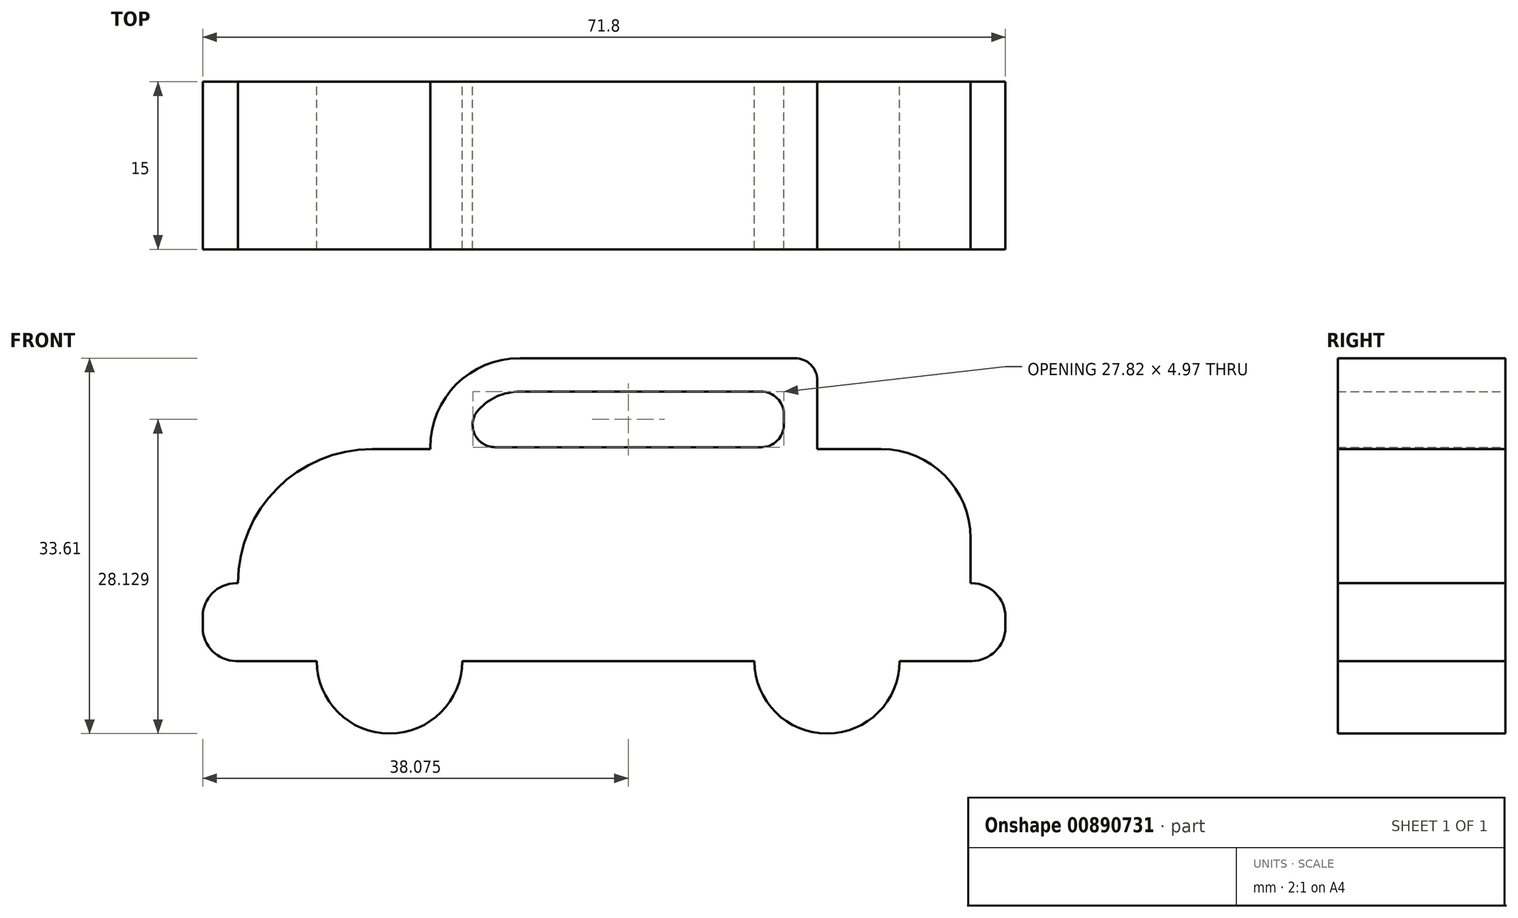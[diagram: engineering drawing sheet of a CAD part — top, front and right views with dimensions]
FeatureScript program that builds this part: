
annotation { "Feature Type Name" : "Feature", "Feature Type Description" : "" }
export const myFeature = defineFeature(function(context is Context, id is Id, definition is map)
    precondition{}
    {
        {
            var Q0;
            Q0=qCreatedBy(makeId("Front.planeOp"),FACE);
            var sketch = newSketch(context, id + "F0", { "sketchPlane" : qUnion([Q0])});
            skLineSegment(sketch, "E0.bottom", {"start": v(-41.37, 0) * mm, "end": v(-34.15, 0) * mm});
            skLineSegment(sketch, "E0.top", {"start": v(-41.37, 6.96) * mm, "end": v(-41.22, 6.96) * mm});
            skLineSegment(sketch, "E0.left", {"start": v(-44.37, 3) * mm, "end": v(-44.37, 3.96) * mm});
            skLineSegment(sketch, "E0.right", {"start": v(27.43, 3) * mm, "end": v(27.43, 3.96) * mm});
            skLineSegment(sketch, "E1", {"start": v(-41.22, 6.96) * mm, "end": v(-41.22, 6.97) * mm});
            skLineSegment(sketch, "E2", {"start": v(-29.22, 18.97) * mm, "end": v(-24.01, 18.97) * mm});
            skLineSegment(sketch, "E3", {"start": v(-24.01, 18.97) * mm, "end": v(-24.01, 19.11) * mm});
            skLineSegment(sketch, "E4", {"start": v(-16.01, 27.11) * mm, "end": v(8.62, 27.11) * mm});
            skLineSegment(sketch, "E5", {"start": v(10.62, 25.11) * mm, "end": v(10.62, 18.97) * mm});
            skLineSegment(sketch, "E6", {"start": v(10.62, 18.97) * mm, "end": v(16.33, 18.97) * mm});
            skLineSegment(sketch, "E7", {"start": v(24.33, 10.97) * mm, "end": v(24.33, 6.96) * mm});
            skLineSegment(sketch, "E8.trimOffspring", {"start": v(24.33, 6.96) * mm, "end": v(24.43, 6.96) * mm});
            skArc(sketch, "E9", {"start": v(-34.15, 0) * mm, "mid": v(-27.65, -6.5) * mm, "end": v(-21.15, 0) * mm});
            skArc(sketch, "E10", {"start": v(4.98, 0) * mm, "mid": v(11.48, -6.5) * mm, "end": v(17.98, 0) * mm});
            skLineSegment(sketch, "E11.trimOffspring", {"start": v(-21.15, 0) * mm, "end": v(4.98, 0) * mm});
            skLineSegment(sketch, "E12.trimOffspring", {"start": v(17.98, 0) * mm, "end": v(24.43, 0) * mm});
            skPoint(sketch, "E13.visualSharp", {"position": v(-44.37, 0) * mm});
            skArc(sketch, "E13.filletArc", {"start": v(-44.37, 3) * mm, "mid": v(-43.5, 0.88) * mm, "end": v(-41.37, 0) * mm});
            skPoint(sketch, "E14.visualSharp", {"position": v(-44.37, 6.96) * mm});
            skArc(sketch, "E14.filletArc", {"start": v(-41.37, 6.96) * mm, "mid": v(-43.5, 6.09) * mm, "end": v(-44.37, 3.96) * mm});
            skPoint(sketch, "E15.visualSharp", {"position": v(27.43, 0) * mm});
            skArc(sketch, "E15.filletArc", {"start": v(24.43, 0) * mm, "mid": v(26.55, 0.88) * mm, "end": v(27.43, 3) * mm});
            skPoint(sketch, "E16.visualSharp", {"position": v(-41.22, 18.97) * mm});
            skArc(sketch, "E16.filletArc", {"start": v(-29.22, 18.97) * mm, "mid": v(-37.7, 15.46) * mm, "end": v(-41.22, 6.97) * mm});
            skPoint(sketch, "E17.visualSharp", {"position": v(27.43, 6.96) * mm});
            skArc(sketch, "E17.filletArc", {"start": v(27.43, 3.96) * mm, "mid": v(26.55, 6.09) * mm, "end": v(24.43, 6.96) * mm});
            skPoint(sketch, "E18.visualSharp", {"position": v(24.33, 18.97) * mm});
            skArc(sketch, "E18.filletArc", {"start": v(24.33, 10.97) * mm, "mid": v(22, 16.63) * mm, "end": v(16.33, 18.97) * mm});
            skPoint(sketch, "E19.visualSharp", {"position": v(-24.01, 27.11) * mm});
            skArc(sketch, "E19.filletArc", {"start": v(-16.01, 27.11) * mm, "mid": v(-21.67, 24.77) * mm, "end": v(-24.01, 19.11) * mm});
            skPoint(sketch, "E20.visualSharp", {"position": v(10.62, 27.11) * mm});
            skArc(sketch, "E20.filletArc", {"start": v(10.62, 25.11) * mm, "mid": v(10.03, 26.53) * mm, "end": v(8.62, 27.11) * mm});
            skArc(sketch, "E21.0", {"start": v(-16.01, 24.11) * mm, "mid": v(-18.02, 23.7) * mm, "end": v(-19.7, 22.5) * mm});
            skLineSegment(sketch, "E21.1", {"start": v(-16.01, 24.11) * mm, "end": v(5.62, 24.11) * mm});
            skLineSegment(sketch, "E21.2", {"start": v(7.62, 22.11) * mm, "end": v(7.62, 21.14) * mm});
            skLineSegment(sketch, "E22", {"start": v(-18.22, 19.14) * mm, "end": v(5.62, 19.14) * mm});
            skPoint(sketch, "E23.visualSharp", {"position": v(7.62, 24.11) * mm});
            skArc(sketch, "E23.filletArc", {"start": v(7.62, 22.11) * mm, "mid": v(7.03, 23.53) * mm, "end": v(5.62, 24.11) * mm});
            skPoint(sketch, "E24.visualSharp", {"position": v(7.62, 19.14) * mm});
            skArc(sketch, "E24.filletArc", {"start": v(5.62, 19.14) * mm, "mid": v(7.03, 19.73) * mm, "end": v(7.62, 21.14) * mm});
            skPoint(sketch, "E25.visualSharp", {"position": v(-21.01, 19.14) * mm});
            skArc(sketch, "E25.filletArc", {"start": v(-19.7, 22.5) * mm, "mid": v(-20.05, 20.34) * mm, "end": v(-18.22, 19.14) * mm});
            skSolve(sketch);
        }
        {
            var Q0;
            Q0=makeQuery(id+"F0.imprint","IMPRINT",FACE,{"disambiguationData":[TD([[makeQuery(id+"F0.imprint","IMPRINT",EDGE,{"derivedFrom":sQuery(id+"F0.wireOp",EDGE,"E0.bottom")}),1.0]])]});
            extrude(context, id + "F1", {"entities" : qUnion([Q0]), "depth" : 15 * mm, "offsetDistance" : 25 * mm});
        }
    });
